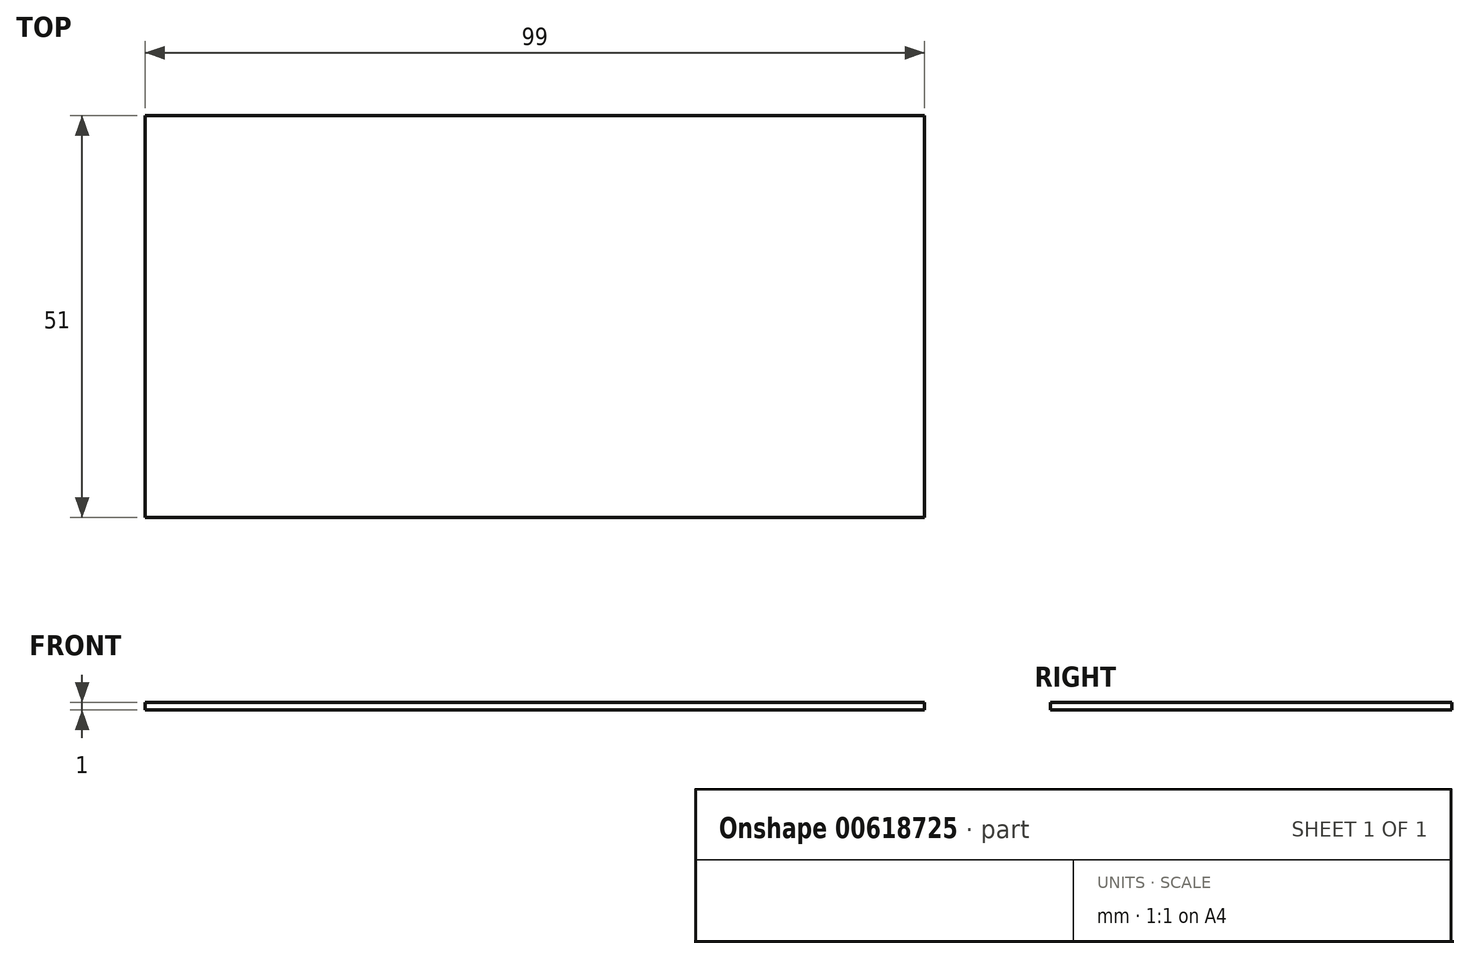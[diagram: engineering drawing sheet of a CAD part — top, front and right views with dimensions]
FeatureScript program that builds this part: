
annotation { "Feature Type Name" : "Feature", "Feature Type Description" : "" }
export const myFeature = defineFeature(function(context is Context, id is Id, definition is map)
    precondition{}
    {
        {
            var Q0;
            Q0=qCreatedBy(makeId("Top.planeOp"),FACE);
            var sketch = newSketch(context, id + "F0", { "sketchPlane" : qUnion([Q0])});
            skLineSegment(sketch, "E0.bottom", {"start": v(-49.5, 25.5) * mm, "end": v(49.5, 25.5) * mm});
            skLineSegment(sketch, "E0.top", {"start": v(-49.5, -25.5) * mm, "end": v(49.5, -25.5) * mm});
            skLineSegment(sketch, "E0.left", {"start": v(-49.5, 25.5) * mm, "end": v(-49.5, -25.5) * mm});
            skLineSegment(sketch, "E0.right", {"start": v(49.5, 25.5) * mm, "end": v(49.5, -25.5) * mm});
            skPoint(sketch, "E0.middle", {"position": v(0, 0) * mm});
            skSolve(sketch);
        }
        {
            var Q0;
            Q0=makeQuery(id+"F0.imprint","IMPRINT",FACE,{"disambiguationData":[TD([[makeQuery(id+"F0.imprint","IMPRINT",EDGE,{"derivedFrom":sQuery(id+"F0.wireOp",EDGE,"E0.bottom")}),-1.0]])]});
            extrude(context, id + "F1", {"entities" : qUnion([Q0]), "depth" : 1 * mm, "offsetDistance" : 25 * mm});
        }
    });
